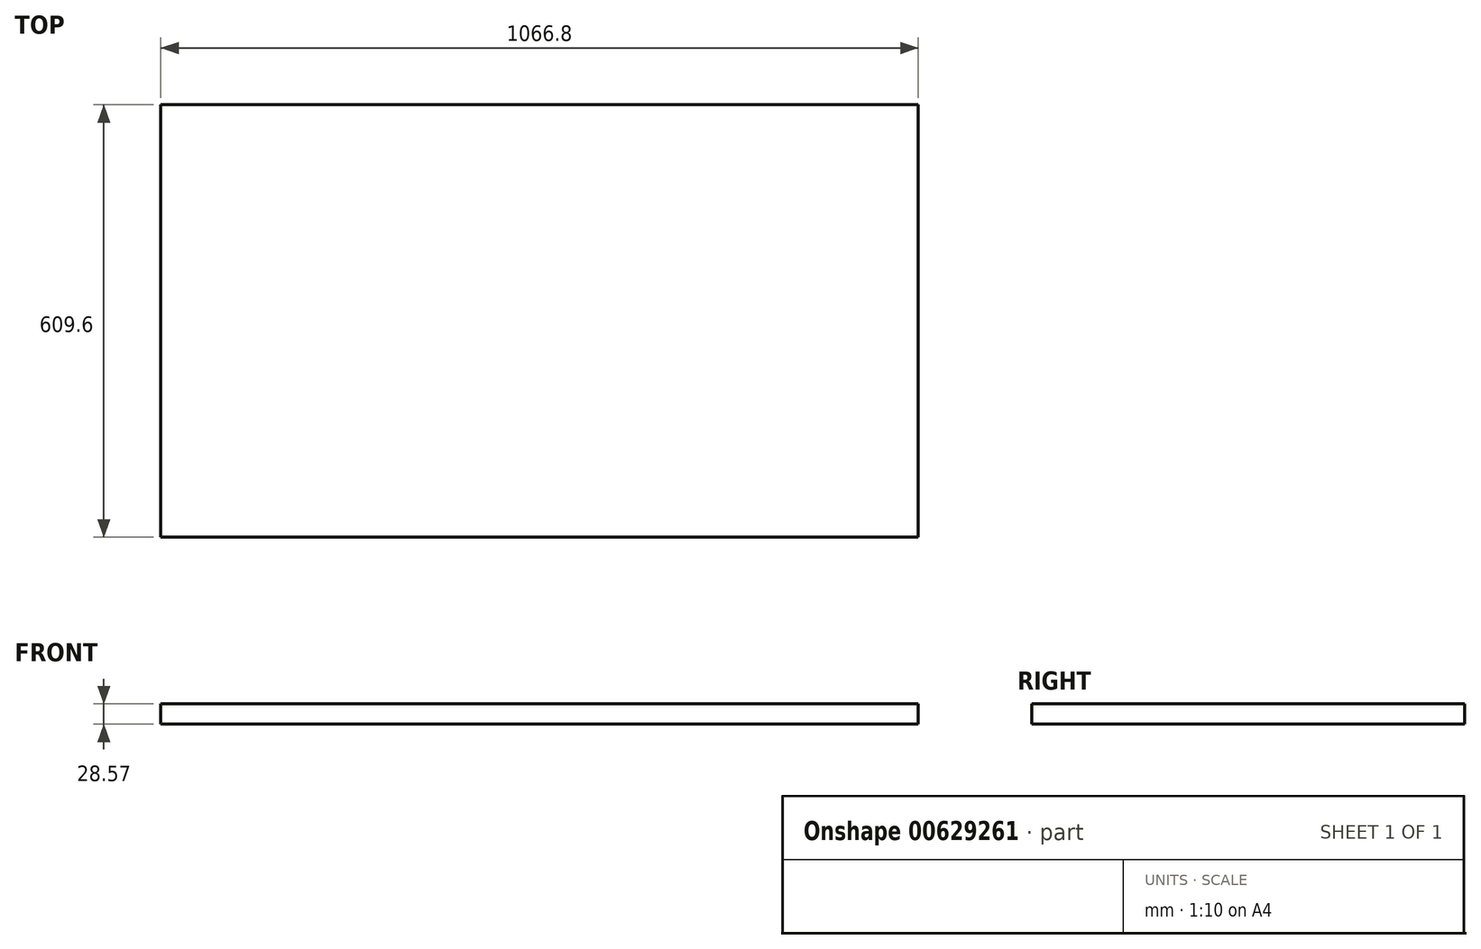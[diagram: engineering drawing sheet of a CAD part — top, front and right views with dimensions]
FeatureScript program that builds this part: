
annotation { "Feature Type Name" : "Feature", "Feature Type Description" : "" }
export const myFeature = defineFeature(function(context is Context, id is Id, definition is map)
    precondition{}
    {
        {
            var Q0;
            Q0=qCreatedBy(makeId("Top.planeOp"),FACE);
            var sketch = newSketch(context, id + "F0", { "sketchPlane" : qUnion([Q0])});
            skLineSegment(sketch, "E0.bottom", {"start": v(-533.4, 304.8) * mm, "end": v(533.4, 304.8) * mm});
            skLineSegment(sketch, "E0.top", {"start": v(-533.4, -304.8) * mm, "end": v(533.4, -304.8) * mm});
            skLineSegment(sketch, "E0.left", {"start": v(-533.4, 304.8) * mm, "end": v(-533.4, -304.8) * mm});
            skLineSegment(sketch, "E0.right", {"start": v(533.4, 304.8) * mm, "end": v(533.4, -304.8) * mm});
            skPoint(sketch, "E0.middle", {"position": v(0, 0) * mm});
            skSolve(sketch);
        }
        {
            var Q0;
            Q0=makeQuery(id+"F0.imprint","IMPRINT",FACE,{"disambiguationData":[TD([[makeQuery(id+"F0.imprint","IMPRINT",EDGE,{"derivedFrom":sQuery(id+"F0.wireOp",EDGE,"E0.bottom")}),-1.0]])]});
            extrude(context, id + "F1", {"entities" : qUnion([Q0]), "depth" : 28.57 * mm, "offsetDistance" : 25.4 * mm});
        }
    });
